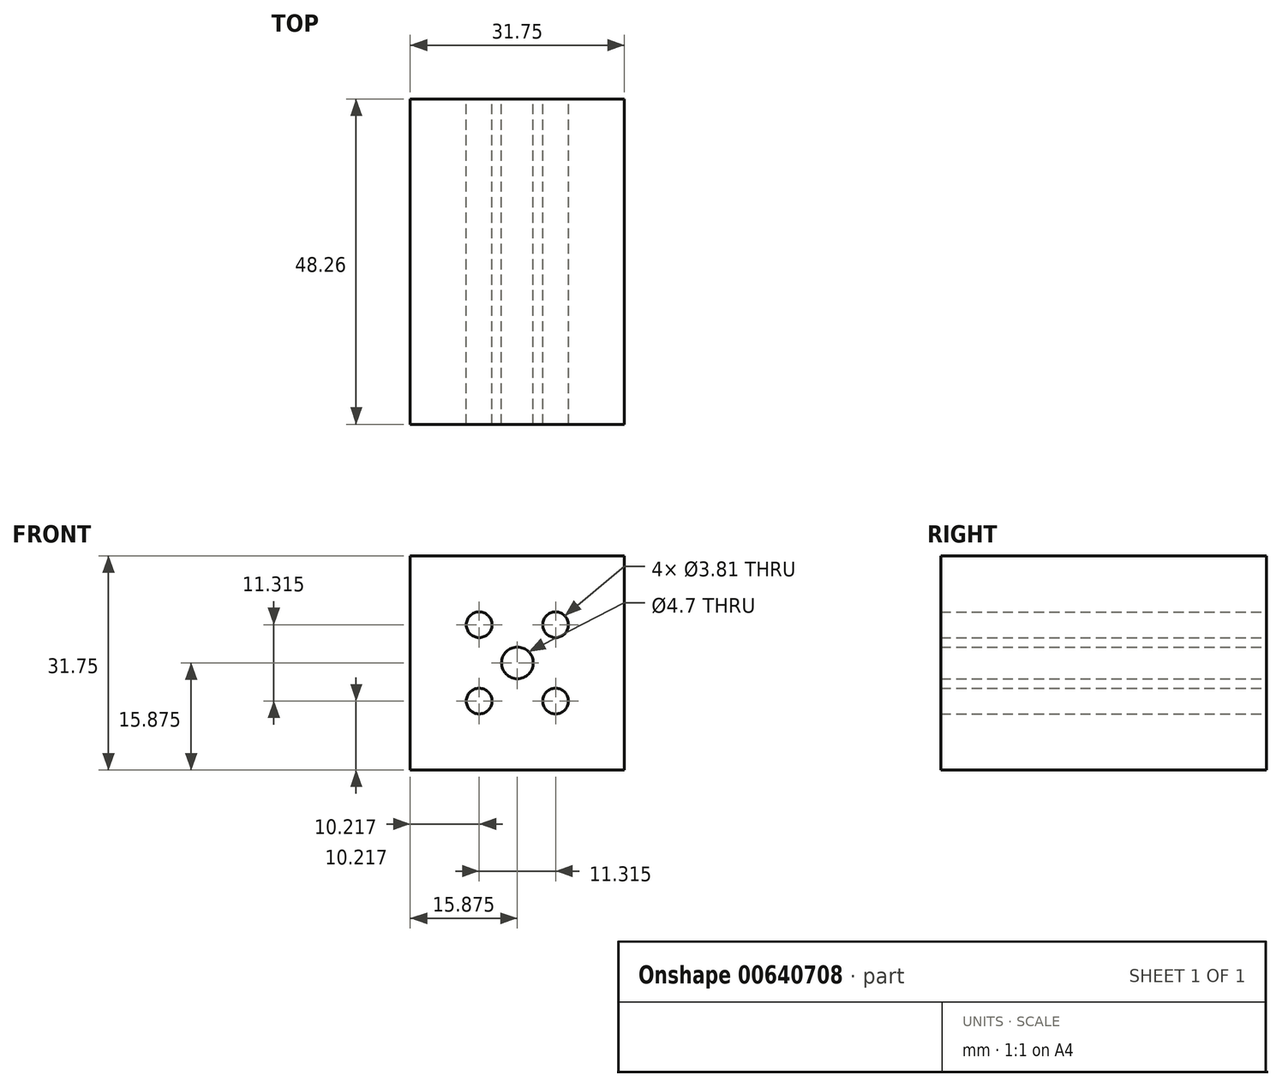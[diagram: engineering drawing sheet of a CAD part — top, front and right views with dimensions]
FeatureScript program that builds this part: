
annotation { "Feature Type Name" : "Feature", "Feature Type Description" : "" }
export const myFeature = defineFeature(function(context is Context, id is Id, definition is map)
    precondition{}
    {
        {
            var Q0;
            Q0=qCreatedBy(makeId("Front.planeOp"),FACE);
            var sketch = newSketch(context, id + "F0", { "sketchPlane" : qUnion([Q0])});
            skLineSegment(sketch, "E0", {"start": v(0, 0) * mm, "end": v(-31.75, 0) * mm});
            skLineSegment(sketch, "E1", {"start": v(-31.75, 0) * mm, "end": v(-31.75, 31.75) * mm});
            skLineSegment(sketch, "E2", {"start": v(-31.75, 31.75) * mm, "end": v(0, 31.75) * mm});
            skLineSegment(sketch, "E3", {"start": v(0, 31.75) * mm, "end": v(0, 0) * mm});
            skCircle(sketch, "E4", {"center": v(-15.88, 15.88) * mm, "radius": 2.35 * mm});
            skPoint(sketch, "E4.centerSnap0", {"position": v(-31.75, 15.88) * mm});
            skPoint(sketch, "E4.centerSnap1", {"position": v(-15.88, 31.75) * mm});
            skCircle(sketch, "E5", {"center": v(-10.22, 21.53) * mm, "radius": 1.9 * mm});
            skCircle(sketch, "E6.1.0", {"center": v(-21.53, 21.53) * mm, "radius": 1.9 * mm});
            skCircle(sketch, "E6.2.0", {"center": v(-21.53, 10.22) * mm, "radius": 1.9 * mm});
            skCircle(sketch, "E6.3.0", {"center": v(-10.22, 10.22) * mm, "radius": 1.9 * mm});
            skSolve(sketch);
        }
        {
            var Q0;
            Q0=makeQuery(id+"F0.imprint","IMPRINT",FACE,{"disambiguationData":[TD([[makeQuery(id+"F0.imprint","IMPRINT",EDGE,{"derivedFrom":sQuery(id+"F0.wireOp",EDGE,"E0")}),-1.0]])]});
            extrude(context, id + "F1", {"entities" : qUnion([Q0]), "depth" : 48.26 * mm, "offsetDistance" : 25.4 * mm});
        }
    });
